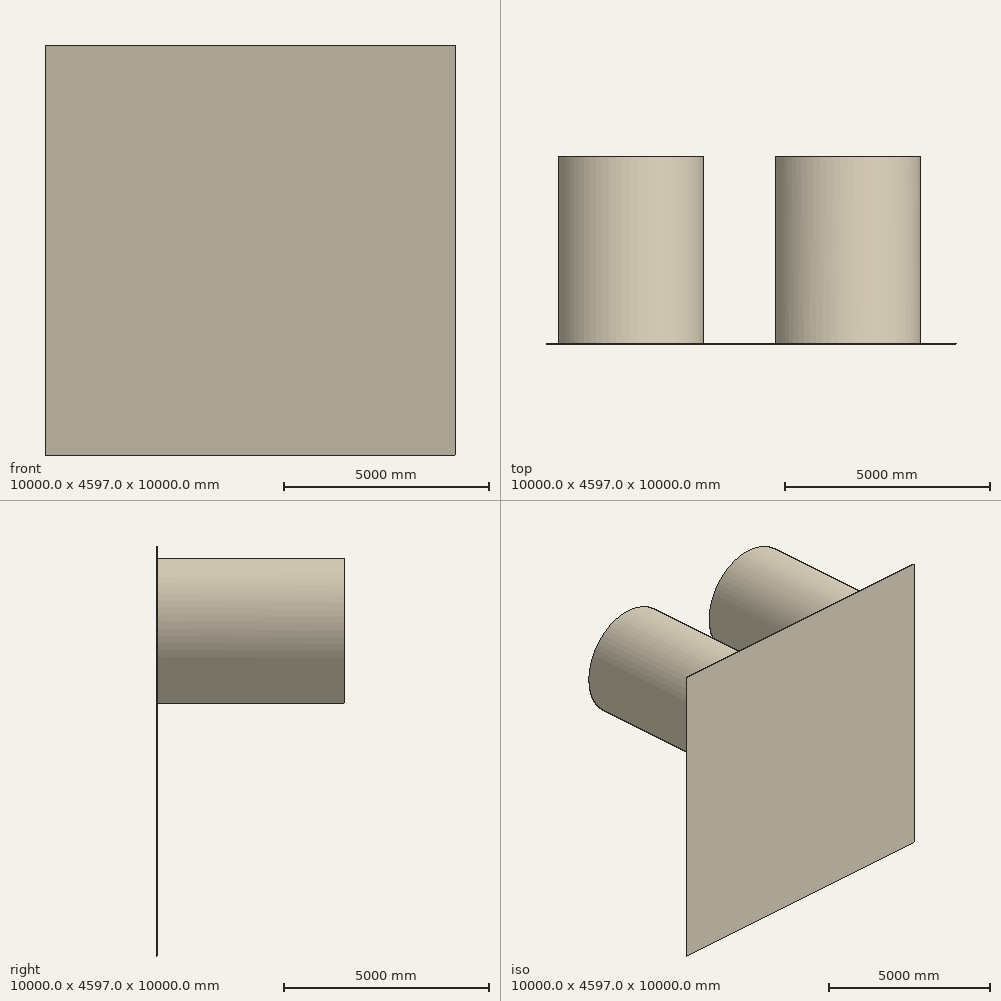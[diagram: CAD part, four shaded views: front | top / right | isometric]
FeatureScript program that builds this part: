
annotation { "Feature Type Name" : "Feature", "Feature Type Description" : "" }
export const myFeature = defineFeature(function(context is Context, id is Id, definition is map)
    precondition{}
    {
        {
            var Q0;
            Q0=qCreatedBy(makeId("Front.planeOp"),FACE);
            var sketch = newSketch(context, id + "F0", { "sketchPlane" : qUnion([Q0])});
            skLineSegment(sketch, "E0.bottom", {"start": v(0, 0) * mm, "end": v(-10000, 0) * mm});
            skLineSegment(sketch, "E0.top", {"start": v(0, 10000) * mm, "end": v(-10000, 10000) * mm});
            skLineSegment(sketch, "E0.left", {"start": v(0, 0) * mm, "end": v(0, 10000) * mm});
            skLineSegment(sketch, "E0.right", {"start": v(-10000, 0) * mm, "end": v(-10000, 10000) * mm});
            skSolve(sketch);
        }
        {
            var Q0;
            Q0=makeQuery(id+"F0.imprint","IMPRINT",FACE,{"disambiguationData":[TD([[makeQuery(id+"F0.imprint","IMPRINT",EDGE,{"derivedFrom":sQuery(id+"F0.wireOp",EDGE,"E0.bottom")}),-1.0]])]});
            extrude(context, id + "F1", {"entities" : qUnion([Q0]), "depth" : 25 * mm, "offsetDistance" : 25 * mm});
        }
        {
            var Q0;
            Q0=makeQuery(id+"F1.opExtrude","CAP_FACE",FACE,{"disambiguationData":[OSD([sQuery(id+"F0.wireOp",EDGE,"E0.bottom"),sQuery(id+"F0.wireOp",EDGE,"E0.top"),sQuery(id+"F0.wireOp",EDGE,"E0.left"),sQuery(id+"F0.wireOp",EDGE,"E0.right")])],"isStart":true});
            var sketch = newSketch(context, id + "F2", { "sketchPlane" : qUnion([Q0])});
            skCircle(sketch, "E1", {"center": v(7942, 7942) * mm, "radius": 1764.5 * mm});
            skCircle(sketch, "E2", {"center": v(2648, 7942) * mm, "radius": 1764.5 * mm});
            skSolve(sketch);
        }
        {
            var Q0;
            Q0=makeQuery(id+"F2.imprint","IMPRINT",FACE,{"disambiguationData":[TD([[makeQuery(id+"F2.imprint","IMPRINT",EDGE,{"derivedFrom":sQuery(id+"F2.wireOp",EDGE,"E2")}),1.0]])]});
            var Q1;
            Q1=makeQuery(id+"F2.imprint","IMPRINT",FACE,{"disambiguationData":[TD([[makeQuery(id+"F2.imprint","IMPRINT",EDGE,{"derivedFrom":sQuery(id+"F2.wireOp",EDGE,"E1")}),1.0]])]});
            var Q2;
            Q2=makeQuery(id+"F2.imprint","IMPRINT",FACE,{"disambiguationData":[TD([[makeQuery(id+"F2.imprint","IMPRINT",EDGE,{"derivedFrom":sQuery(id+"F2.wireOp",EDGE,"54be989f-5d2a-44d5-bde4-370c4e6ceba00.MirrorC")}),-1.0]])]});
            extrude(context, id + "F3", {"entities" : qUnion([Q0, Q1, Q2]), "operationType" : NewBodyOperationType.ADD, "depth" : 4572 * mm, "offsetDistance" : 25 * mm});
        }
    });
